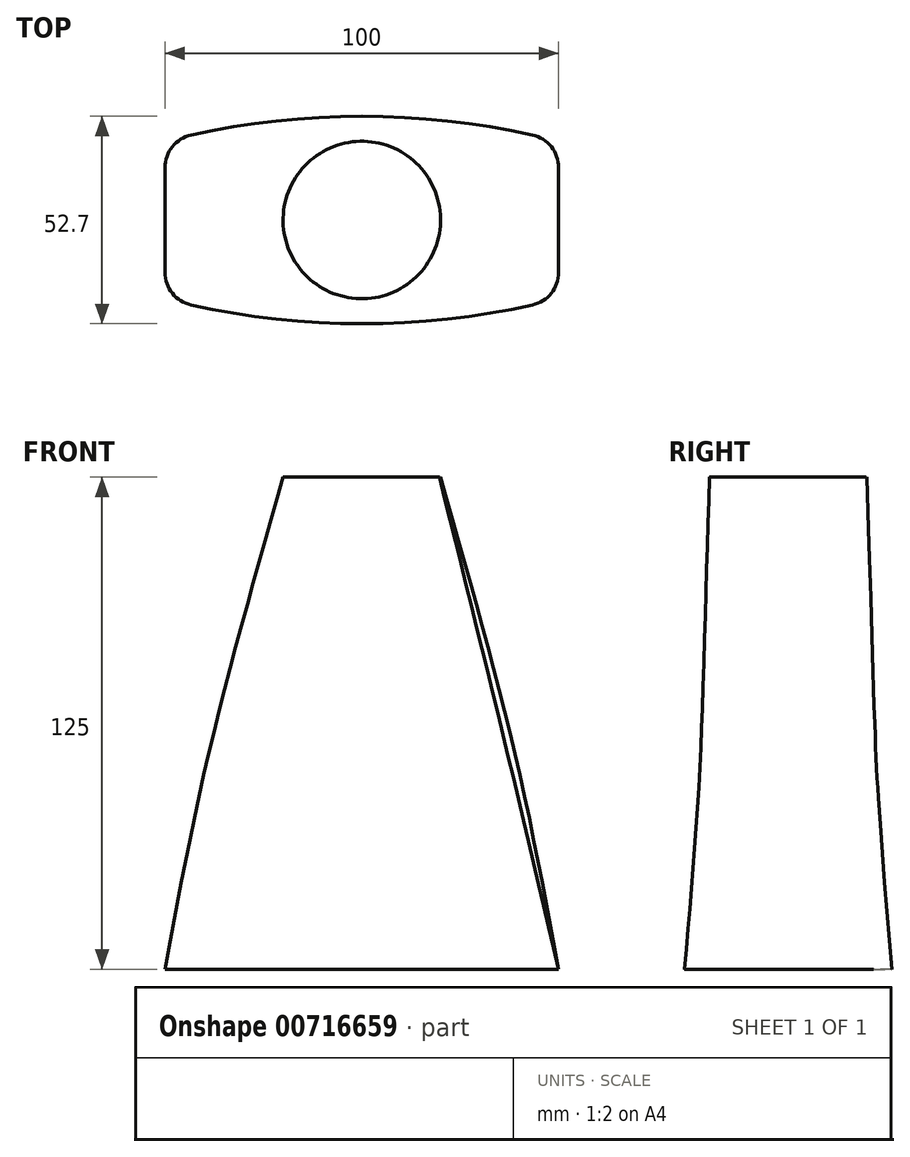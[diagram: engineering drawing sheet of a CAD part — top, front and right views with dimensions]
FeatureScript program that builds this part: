
annotation { "Feature Type Name" : "Feature", "Feature Type Description" : "" }
export const myFeature = defineFeature(function(context is Context, id is Id, definition is map)
    precondition{}
    {
        {
            var Q0;
            Q0=qCreatedBy(makeId("Top.planeOp"),FACE);
            var sketch = newSketch(context, id + "F0", { "sketchPlane" : qUnion([Q0])});
            skLineSegment(sketch, "E0.bottom", {"start": v(50, -20) * mm, "end": v(-50, -20) * mm, "construction": true});
            skLineSegment(sketch, "E0.left", {"start": v(50, -13.3) * mm, "end": v(50, 13.3) * mm});
            skLineSegment(sketch, "E0.right", {"start": v(-50, -13.3) * mm, "end": v(-50, 13.3) * mm});
            skPoint(sketch, "E0.middle", {"position": v(0, 0) * mm});
            skArc(sketch, "E1", {"start": v(43.34, 21.6) * mm, "mid": v(0, 26.35) * mm, "end": v(-43.34, 21.6) * mm});
            skArc(sketch, "E2", {"start": v(-43.34, -21.6) * mm, "mid": v(0, -26.35) * mm, "end": v(43.34, -21.6) * mm});
            skLineSegment(sketch, "E3", {"start": v(50, 20) * mm, "end": v(-50, 20) * mm, "construction": true});
            skPoint(sketch, "E4.visualSharp", {"position": v(50, 20) * mm});
            skArc(sketch, "E4.filletArc", {"start": v(50, 13.3) * mm, "mid": v(48.13, 18.62) * mm, "end": v(43.34, 21.6) * mm});
            skPoint(sketch, "E5.visualSharp", {"position": v(50, -20) * mm});
            skArc(sketch, "E5.filletArc", {"start": v(43.34, -21.6) * mm, "mid": v(48.13, -18.62) * mm, "end": v(50, -13.3) * mm});
            skPoint(sketch, "E6.visualSharp", {"position": v(-50, -20) * mm});
            skArc(sketch, "E6.filletArc", {"start": v(-50, -13.3) * mm, "mid": v(-48.13, -18.62) * mm, "end": v(-43.34, -21.6) * mm});
            skPoint(sketch, "E7.visualSharp", {"position": v(-50, 20) * mm});
            skArc(sketch, "E7.filletArc", {"start": v(-43.34, 21.6) * mm, "mid": v(-48.13, 18.62) * mm, "end": v(-50, 13.3) * mm});
            skSolve(sketch);
        }
        {
            var Q0;
            Q0=qCreatedBy(makeId("Top.planeOp"),FACE);
            cPlane(context, id + "F1", {"entities" : qUnion([Q0]), "cplaneType" : CPlaneType.OFFSET, "offset" : 50 * mm, "width" : 150 * mm, "height" : 150 * mm});
        }
        {
            var Q0;
            Q0=qCreatedBy(id+"F1.planeOp",FACE);
            var sketch = newSketch(context, id + "F2", { "sketchPlane" : qUnion([Q0])});
            skEllipse(sketch, "E8", {"center": v(0, 0) * mm, "majorRadius": 40 * mm, "minorRadius": 22.5 * mm, "majorAxis": v(-1, 0)});
            skSolve(sketch);
        }
        {
            var Q0;
            Q0=qCreatedBy(makeId("Top.planeOp"),FACE);
            cPlane(context, id + "F3", {"entities" : qUnion([Q0]), "cplaneType" : CPlaneType.OFFSET, "offset" : 125 * mm, "width" : 150 * mm, "height" : 150 * mm});
        }
        {
            var Q0;
            Q0=qCreatedBy(id+"F3.planeOp",FACE);
            var sketch = newSketch(context, id + "F4", { "sketchPlane" : qUnion([Q0])});
            skCircle(sketch, "E9", {"center": v(0, 0) * mm, "radius": 20 * mm});
            skSolve(sketch);
        }
        {
            var Q0;
            Q0=makeQuery(id+"F0.imprint","IMPRINT",FACE,{"disambiguationData":[TD([[makeQuery(id+"F0.imprint","IMPRINT",EDGE,{"derivedFrom":sQuery(id+"F0.wireOp",EDGE,"E0.left")}),1.0]])]});
            var Q1;
            Q1=makeQuery(id+"F2.imprint","IMPRINT",FACE,{"disambiguationData":[TD([[makeQuery(id+"F2.imprint","IMPRINT",EDGE,{"derivedFrom":sQuery(id+"F2.wireOp",EDGE,"E8")}),1.0]])]});
            var Q2;
            Q2=makeQuery(id+"F4.imprint","IMPRINT",FACE,{"disambiguationData":[TD([[makeQuery(id+"F4.imprint","IMPRINT",EDGE,{"derivedFrom":sQuery(id+"F4.wireOp",EDGE,"E9")}),1.0]])]});
            loft(context, id + "F5", {"sheetProfilesArray" : [{ "sheetProfileEntities" : qUnion([Q0]) }, { "sheetProfileEntities" : qUnion([Q1]) }, { "sheetProfileEntities" : qUnion([Q2]) }]});
        }
    });
